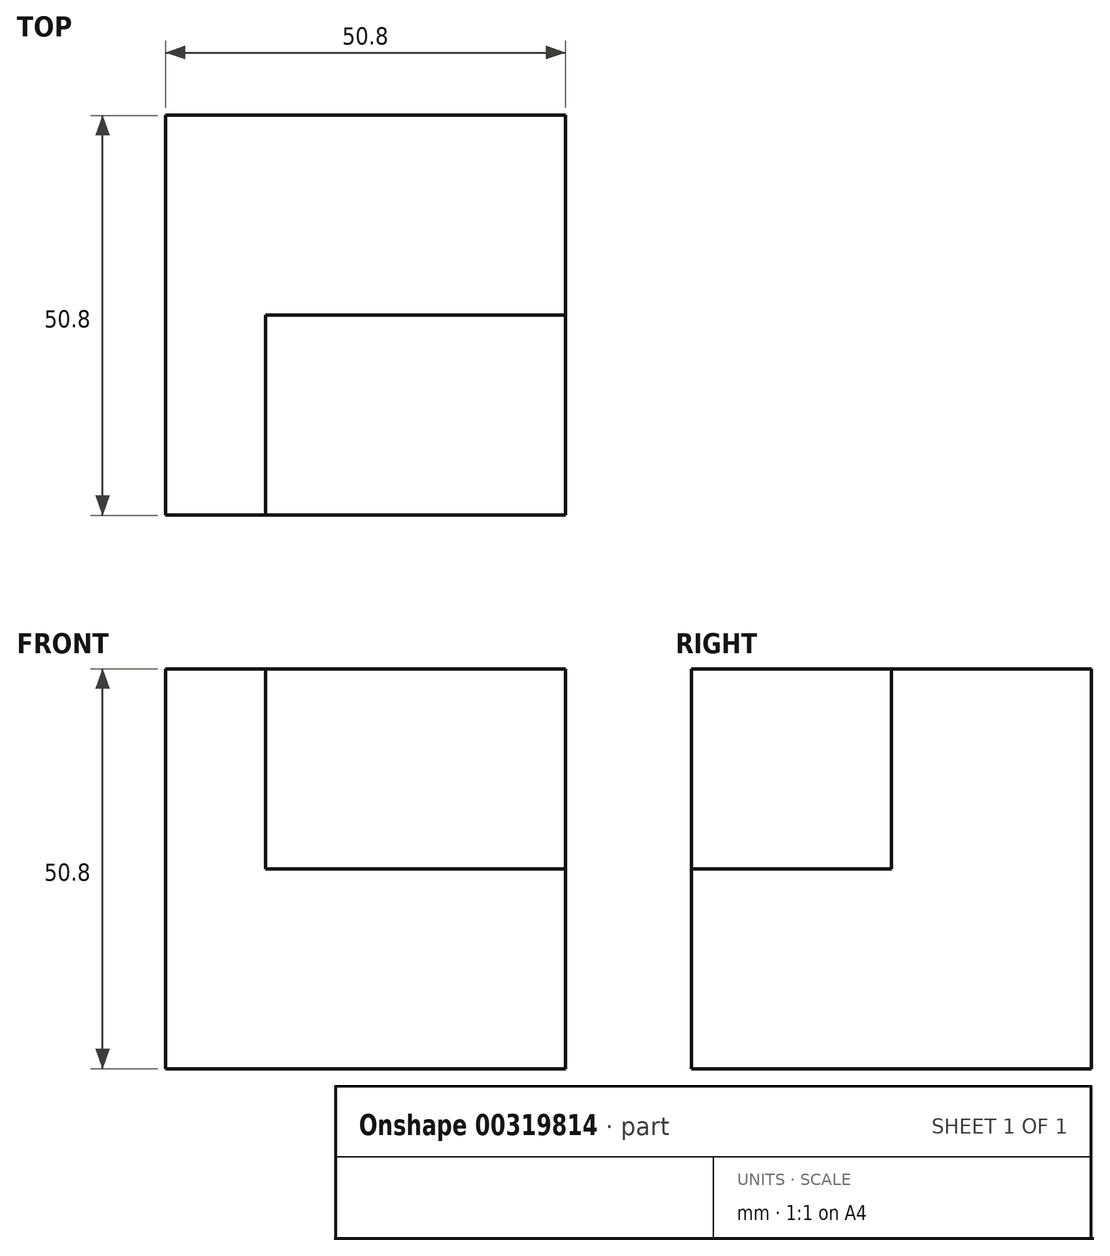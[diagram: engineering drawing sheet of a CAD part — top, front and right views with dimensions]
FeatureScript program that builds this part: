
annotation { "Feature Type Name" : "Feature", "Feature Type Description" : "" }
export const myFeature = defineFeature(function(context is Context, id is Id, definition is map)
    precondition{}
    {
        {
            var Q0;
            Q0=qCreatedBy(makeId("Top.planeOp"),FACE);
            var sketch = newSketch(context, id + "F0", { "sketchPlane" : qUnion([Q0])});
            skLineSegment(sketch, "E0.bottom", {"start": v(-18.17, 31.11) * mm, "end": v(32.63, 31.11) * mm});
            skLineSegment(sketch, "E0.top", {"start": v(-18.17, -19.69) * mm, "end": v(32.63, -19.69) * mm});
            skLineSegment(sketch, "E0.left", {"start": v(-18.17, 31.11) * mm, "end": v(-18.17, -19.69) * mm});
            skLineSegment(sketch, "E0.right", {"start": v(32.63, 31.11) * mm, "end": v(32.63, -19.69) * mm});
            skSolve(sketch);
        }
        {
            var Q0;
            Q0=makeQuery(id+"F0.imprint","IMPRINT",FACE,{"disambiguationData":[TD([[makeQuery(id+"F0.imprint","IMPRINT",EDGE,{"derivedFrom":sQuery(id+"F0.wireOp",EDGE,"E0.bottom")}),-1.0]])]});
            extrude(context, id + "F1", {"entities" : qUnion([Q0]), "oppositeDirection" : true, "depth" : 50.8 * mm});
        }
        {
            var Q0;
            Q0=makeQuery(id+"F1.opExtrude","CAP_FACE",FACE,{"disambiguationData":[OSD([sQuery(id+"F0.wireOp",EDGE,"E0.bottom"),sQuery(id+"F0.wireOp",EDGE,"E0.top"),sQuery(id+"F0.wireOp",EDGE,"E0.left"),sQuery(id+"F0.wireOp",EDGE,"E0.right")])],"isStart":true});
            var sketch = newSketch(context, id + "F2", { "sketchPlane" : qUnion([Q0])});
            skLineSegment(sketch, "E1", {"start": v(32.63, -19.69) * mm, "end": v(32.63, 5.71) * mm});
            skLineSegment(sketch, "E2", {"start": v(32.63, 5.71) * mm, "end": v(-5.47, 5.71) * mm});
            skLineSegment(sketch, "E3", {"start": v(-5.47, 5.71) * mm, "end": v(-5.47, -19.69) * mm});
            skLineSegment(sketch, "E4", {"start": v(-5.47, -19.69) * mm, "end": v(32.63, -19.69) * mm});
            skSolve(sketch);
        }
        {
            var Q0;
            Q0=makeQuery(id+"F2.imprint","IMPRINT",FACE,{"disambiguationData":[TD([[makeQuery(id+"F2.imprint","IMPRINT",EDGE,{"derivedFrom":sQuery(id+"F2.wireOp",EDGE,"E1")}),-1.0]])]});
            extrude(context, id + "F3", {"entities" : qUnion([Q0]), "operationType" : NewBodyOperationType.REMOVE, "oppositeDirection" : true, "depth" : 25.4 * mm});
        }
    });
